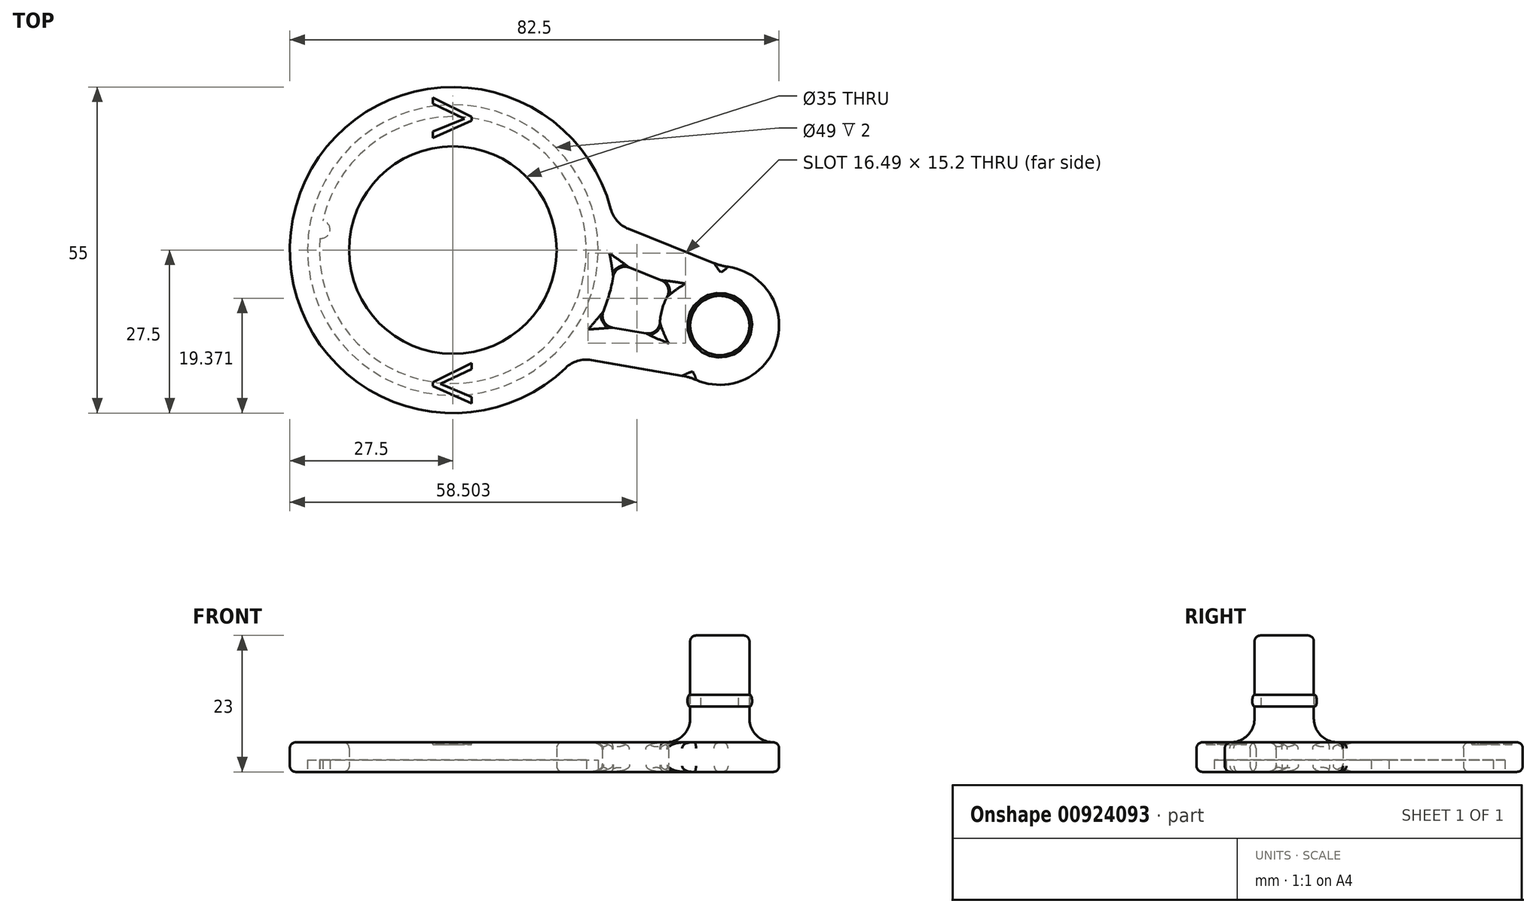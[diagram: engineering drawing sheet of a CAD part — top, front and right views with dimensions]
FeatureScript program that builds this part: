
annotation { "Feature Type Name" : "Feature", "Feature Type Description" : "" }
export const myFeature = defineFeature(function(context is Context, id is Id, definition is map)
    precondition{}
    {
        {
            var Q0;
            Q0=qCreatedBy(makeId("Top.planeOp"),FACE);
            var sketch = newSketch(context, id + "F0", { "sketchPlane" : qUnion([Q0])});
            skLineSegment(sketch, "E0.1", {"start": v(6.5, -1.84) * mm, "end": v(6.5, -1.9) * mm});
            skLineSegment(sketch, "E1", {"start": v(0, 0) * mm, "end": v(81.74, -23.12) * mm, "construction": true});
            skArc(sketch, "E2", {"start": v(40.08, -21.44) * mm, "mid": v(54.62, -15.45) * mm, "end": v(45.37, -2.74) * mm});
            skPoint(sketch, "E3", {"position": v(40.08, -21.44) * mm});
            skLineSegment(sketch, "E4", {"start": v(40.08, -21.44) * mm, "end": v(23.33, -18.54) * mm});
            skPoint(sketch, "E5", {"position": v(45.37, -2.74) * mm});
            skLineSegment(sketch, "E6", {"start": v(45.37, -2.74) * mm, "end": v(29.59, 3.58) * mm});
            skArc(sketch, "E7", {"start": v(26.6, 6.95) * mm, "mid": v(-26.46, 7.48) * mm, "end": v(19.02, -19.86) * mm});
            skPoint(sketch, "E8.visualSharp", {"position": v(27.12, 4.56) * mm});
            skArc(sketch, "E8.filletArc", {"start": v(26.6, 6.95) * mm, "mid": v(27.7, 4.91) * mm, "end": v(29.59, 3.58) * mm});
            skPoint(sketch, "E9.visualSharp", {"position": v(20.71, -18.1) * mm});
            skArc(sketch, "E9.filletArc", {"start": v(23.33, -18.54) * mm, "mid": v(21.02, -18.69) * mm, "end": v(19.02, -19.86) * mm});
            skCircle(sketch, "E10", {"center": v(0, 0) * mm, "radius": 17.5 * mm});
            skArc(sketch, "E11", {"start": v(24.31, -12.63) * mm, "mid": v(26.36, -7.46) * mm, "end": v(27.32, -1.98) * mm});
            skArc(sketch, "E12", {"start": v(37.44, -6.03) * mm, "mid": v(35.28, -9.98) * mm, "end": v(35.05, -14.48) * mm});
            skLineSegment(sketch, "E13", {"start": v(27.32, -1.98) * mm, "end": v(37.44, -6.03) * mm});
            skLineSegment(sketch, "E14", {"start": v(24.31, -12.63) * mm, "end": v(35.05, -14.48) * mm});
            skSolve(sketch);
        }
        {
            var Q0;
            Q0 = qSketchRegion(id + "F0", true);
            extrude(context, id + "F1", {"entities" : qUnion([Q0]), "depth" : 5 * mm, "offsetDistance" : 25 * mm});
        }
        {
            var Q0;
            Q0=qCreatedBy(makeId("Top.planeOp"),FACE);
            var sketch = newSketch(context, id + "F2", { "sketchPlane" : qUnion([Q0])});
            skCircle(sketch, "E15", {"center": v(0, 0) * mm, "radius": 17.5 * mm});
            skLineSegment(sketch, "E16", {"start": v(-32.86, 0) * mm, "end": v(78.2, 0) * mm});
            skSolve(sketch);
        }
        {
            var Q0;
            Q0 = qSketchRegion(id + "F2", true);
            extrude(context, id + "F3", {"entities" : qUnion([Q0]), "operationType" : NewBodyOperationType.REMOVE, "oppositeDirection" : true, "depth" : 25 * mm, "offsetDistance" : 25 * mm, "symmetric" : true});
        }
        {
            var Q0;
            Q0=qCreatedBy(makeId("Top.planeOp"),FACE);
            var sketch = newSketch(context, id + "F4", { "sketchPlane" : qUnion([Q0])});
            skCircle(sketch, "E17", {"center": v(45, -12.73) * mm, "radius": 5 * mm});
            skSolve(sketch);
        }
        {
            var Q0;
            Q0 = qSketchRegion(id + "F4", true);
            extrude(context, id + "F5", {"entities" : qUnion([Q0]), "operationType" : NewBodyOperationType.ADD, "depth" : 23 * mm, "offsetDistance" : 25 * mm});
        }
        {
            var Q0;
            Q0=makeQuery(id+"F5.boolean.opBoolean","INTERSECT",EDGE,{"derivedFrom":[makeQuery(id+"F1.opExtrude","CAP_FACE",FACE,{"disambiguationData":[OSD([sQuery(id+"F0.wireOp",EDGE,"E2"),sQuery(id+"F0.wireOp",EDGE,"E4"),sQuery(id+"F0.wireOp",EDGE,"E6"),sQuery(id+"F0.wireOp",EDGE,"E7"),sQuery(id+"F0.wireOp",EDGE,"E8.filletArc"),sQuery(id+"F0.wireOp",EDGE,"E9.filletArc"),sQuery(id+"F0.wireOp",EDGE,"E10"),sQuery(id+"F0.wireOp",EDGE,"E11"),sQuery(id+"F0.wireOp",EDGE,"E12"),sQuery(id+"F0.wireOp",EDGE,"E13"),sQuery(id+"F0.wireOp",EDGE,"E14")])],"isStart":false}),makeQuery(id+"F5.opExtrude","SWEPT_FACE",FACE,{"disambiguationData":[OSD([sQuery(id+"F4.wireOp",EDGE,"E17")])]})]});
            fillet(context, id + "F6", {"entities" : qUnion([Q0]), "radius" : 4 * mm, "tangentPropagation" : true, "allowEdgeOverflow" : false});
        }
        {
            var Q0;
            Q0=makeQuery(id+"F1.opExtrude","CAP_FACE",FACE,{"disambiguationData":[OSD([sQuery(id+"F0.wireOp",EDGE,"E2"),sQuery(id+"F0.wireOp",EDGE,"E4"),sQuery(id+"F0.wireOp",EDGE,"E6"),sQuery(id+"F0.wireOp",EDGE,"E7"),sQuery(id+"F0.wireOp",EDGE,"E8.filletArc"),sQuery(id+"F0.wireOp",EDGE,"E9.filletArc"),sQuery(id+"F0.wireOp",EDGE,"E10")])],"isStart":false});
            var Q1;
            Q1=makeQuery(id+"F1.opExtrude","CAP_FACE",FACE,{"disambiguationData":[OSD([sQuery(id+"F0.wireOp",EDGE,"E2"),sQuery(id+"F0.wireOp",EDGE,"E4"),sQuery(id+"F0.wireOp",EDGE,"E6"),sQuery(id+"F0.wireOp",EDGE,"E7"),sQuery(id+"F0.wireOp",EDGE,"E8.filletArc"),sQuery(id+"F0.wireOp",EDGE,"E9.filletArc"),sQuery(id+"F0.wireOp",EDGE,"E10")])],"isStart":true});
            var Q2;
            Q2=makeQuery(id+"F5.opExtrude","CAP_EDGE",EDGE,{"disambiguationData":[OSD([sQuery(id+"F4.wireOp",EDGE,"E17")])],"isStart":false});
            fillet(context, id + "F7", {"entities" : qUnion([Q0, Q1, Q2]), "radius" : 1 * mm, "tangentPropagation" : true, "allowEdgeOverflow" : false});
        }
        {
            var Q0;
            Q0=makeQuery(id+"F1.opExtrude","CAP_FACE",FACE,{"disambiguationData":[OSD([sQuery(id+"F0.wireOp",EDGE,"E2"),sQuery(id+"F0.wireOp",EDGE,"E4"),sQuery(id+"F0.wireOp",EDGE,"E6"),sQuery(id+"F0.wireOp",EDGE,"E7"),sQuery(id+"F0.wireOp",EDGE,"E8.filletArc"),sQuery(id+"F0.wireOp",EDGE,"E9.filletArc"),sQuery(id+"F0.wireOp",EDGE,"E10")])],"isStart":true});
            var sketch = newSketch(context, id + "F8", { "sketchPlane" : qUnion([Q0])});
            skArc(sketch, "E18", {"start": v(-21.95, -4.94) * mm, "mid": v(22.23, 3.47) * mm, "end": v(-22.41, -1.98) * mm});
            skCircle(sketch, "E19", {"center": v(0, 0) * mm, "radius": 24.5 * mm});
            skArc(sketch, "E20", {"start": v(-21.95, -4.94) * mm, "mid": v(-20.75, -3.24) * mm, "end": v(-22.41, -1.98) * mm});
            skSolve(sketch);
        }
        {
            var Q0;
            Q0 = qSketchRegion(id + "F8", true);
            extrude(context, id + "F9", {"entities" : qUnion([Q0]), "operationType" : NewBodyOperationType.REMOVE, "oppositeDirection" : true, "depth" : 2 * mm, "offsetDistance" : 25 * mm});
        }
        {
            var Q0;
            Q0=makeQuery(id+"F1.opExtrude","SWEPT_EDGE",EDGE,{"disambiguationData":[OSD([sQuery(id+"F0.wireOp",EDGE,"E12"),sQuery(id+"F0.wireOp",EDGE,"E13")])]});
            var Q1;
            Q1=makeQuery(id+"F1.opExtrude","SWEPT_EDGE",EDGE,{"disambiguationData":[OSD([sQuery(id+"F0.wireOp",EDGE,"E12"),sQuery(id+"F0.wireOp",EDGE,"E14")])]});
            var Q2;
            Q2=makeQuery(id+"F1.opExtrude","SWEPT_EDGE",EDGE,{"disambiguationData":[OSD([sQuery(id+"F0.wireOp",EDGE,"E11"),sQuery(id+"F0.wireOp",EDGE,"E13")])]});
            var Q3;
            Q3=makeQuery(id+"F1.opExtrude","SWEPT_EDGE",EDGE,{"disambiguationData":[OSD([sQuery(id+"F0.wireOp",EDGE,"E11"),sQuery(id+"F0.wireOp",EDGE,"E14")])]});
            fillet(context, id + "F10", {"entities" : qUnion([Q0, Q1, Q2, Q3]), "radius" : 2 * mm, "tangentPropagation" : true, "allowEdgeOverflow" : false});
        }
        {
            var Q0;
            Q0=makeQuery(id+"F1.opExtrude","SWEPT_EDGE",EDGE,{"disambiguationData":[OSD([sQuery(id+"F0.wireOp",EDGE,"E2"),sQuery(id+"F0.wireOp",EDGE,"E6")])]});
            var Q1;
            Q1=makeQuery(id+"F1.opExtrude","SWEPT_EDGE",EDGE,{"disambiguationData":[OSD([sQuery(id+"F0.wireOp",EDGE,"E2"),sQuery(id+"F0.wireOp",EDGE,"E4")])]});
            fillet(context, id + "F11", {"entities" : qUnion([Q0, Q1]), "radius" : 10 * mm, "tangentPropagation" : true, "allowEdgeOverflow" : false});
        }
        {
            var Q0;
            Q0=makeQuery(id+"F1.opExtrude","CAP_FACE",FACE,{"disambiguationData":[OSD([sQuery(id+"F0.wireOp",EDGE,"E2"),sQuery(id+"F0.wireOp",EDGE,"E4"),sQuery(id+"F0.wireOp",EDGE,"E6"),sQuery(id+"F0.wireOp",EDGE,"E7"),sQuery(id+"F0.wireOp",EDGE,"E8.filletArc"),sQuery(id+"F0.wireOp",EDGE,"E9.filletArc"),sQuery(id+"F0.wireOp",EDGE,"E10"),sQuery(id+"F0.wireOp",EDGE,"E11"),sQuery(id+"F0.wireOp",EDGE,"E12"),sQuery(id+"F0.wireOp",EDGE,"E13"),sQuery(id+"F0.wireOp",EDGE,"E14")])],"isStart":false});
            var sketch = newSketch(context, id + "F12", { "sketchPlane" : qUnion([Q0])});
            skText(sketch, "E21", { "text": "<", "fontName": "OpenSans-Regular.ttf"});
            skText(sketch, "E22", { "text": ">", "fontName": "OpenSans-Regular.ttf"});
            const initialGuessF12  = {"E21": [-0.00406, -0.02747, 1, 0, 0.01], "E22": [-0.00406, 0.0173, 1, 0, 0.01]};
            skSetInitialGuess(sketch, initialGuessF12);
            skSolve(sketch);
        }
        {
            var Q0;
            Q0 = qSketchRegion(id + "F12", true);
            extrude(context, id + "F13", {"entities" : qUnion([Q0]), "operationType" : NewBodyOperationType.REMOVE, "oppositeDirection" : true, "depth" : 0.4 * mm, "offsetDistance" : 25 * mm});
        }
        {
            var Q0;
            Q0=makeQuery(id+"F5.opExtrude","SWEPT_FACE",FACE,{"disambiguationData":[OSD([sQuery(id+"F4.wireOp",EDGE,"E17")])]});
            cPlane(context, id + "F14", {"entities" : qUnion([Q0]), "cplaneType" : CPlaneType.LINE_ANGLE, "offset" : 25 * mm, "angle" : 0 * degree, "width" : 150 * mm, "height" : 150 * mm});
        }
        {
            var Q0;
            Q0=qCreatedBy(id+"F14.planeOp",FACE);
            var sketch = newSketch(context, id + "F15", { "sketchPlane" : qUnion([Q0])});
            skLineSegment(sketch, "E23", {"start": v(17.71, 10.7) * mm, "end": v(17.71, 13) * mm});
            skEllipticalArc(sketch, "E24", {});
            skLineSegment(sketch, "E25", {"start": v(12.67, 27.18) * mm, "end": v(12.67, 4.8) * mm, "construction": true});
            const initialGuessF15  = {"E24": [0.017714622085877173, 0.012, 0, -1, 0.001, 0.0004, 0, 3.141592653589793]};
            skSetInitialGuess(sketch, initialGuessF15);
            skSolve(sketch);
        }
        {
            var Q0;
            Q0 = qSketchRegion(id + "F15", true);
            var Q1;
            {var subQ0=sQuery(id+"F15.wireOp",EDGE,"E24");Q1=makeQuery(id+"F15.imprint","IMPRINT",FACE,{"disambiguationData":[TD([[makeQuery(id+"F15.imprint","IMPRINT",EDGE,{"derivedFrom":subQ0}),1.0]])]});}
            var Q2;
            Q2=sQuery(id+"F15.wireOp",EDGE,"E25");
            revolve(context, id + "F16", {"operationType" : NewBodyOperationType.ADD, "surfaceOperationType" : NewSurfaceOperationType.NEW, "entities" : qUnion([Q0, Q1]), "axis" : qUnion([Q2]), "revolveType" : RevolveType.FULL});
        }
    });
